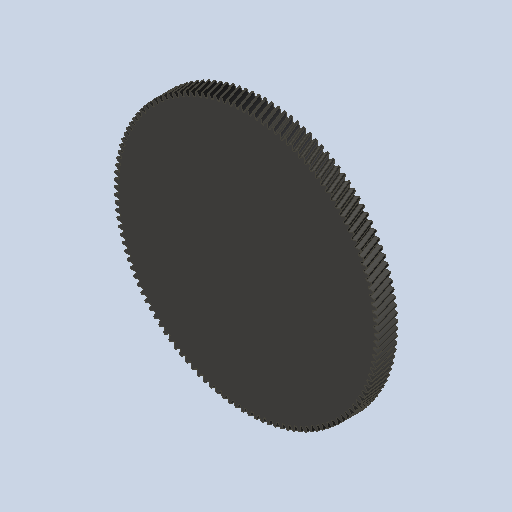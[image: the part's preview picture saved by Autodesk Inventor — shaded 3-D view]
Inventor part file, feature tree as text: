
AUTODESK INVENTOR PART (.ipt)
format: ipt  version: 2023 (Build 270158000, 158)  size: 1,488,384 bytes
history: native  units: mm (DEFAULTED — no unit token found)
features: plane x3, other x3, sketch x2, extrude x1
ambient origin geometry x8: Origin, YZ Plane, XZ Plane, XY Plane, X Axis, Y Axis, Z Axis, Center Point
bodies: Solid1 (feature_tree)
feature tree (9):
  extrude  "Extrusion1"  Depth=10.0mm TaperAngle=0.0deg
  plane  "Work Plane2"
  plane  "Work Plane8"
  plane  "Work Plane9"
  other  "Spur Gear"
  sketch  "Sketch1"  dims[d0=137.150577mm d1=10.0mm d2=0.0mm]
  sketch  "Sketch2"  dims[d3=135.150577mm d4=10.0mm d5=0.0mm d16=101.6mm d17=0.0mm d34=0.24737mm d39=0.0mm d41=0.0mm d43=101.6mm d46=101.6mm d47=0.0mm d48=0.0mm]
  other  "Srf1"
  other  "Pitch Diameter"
